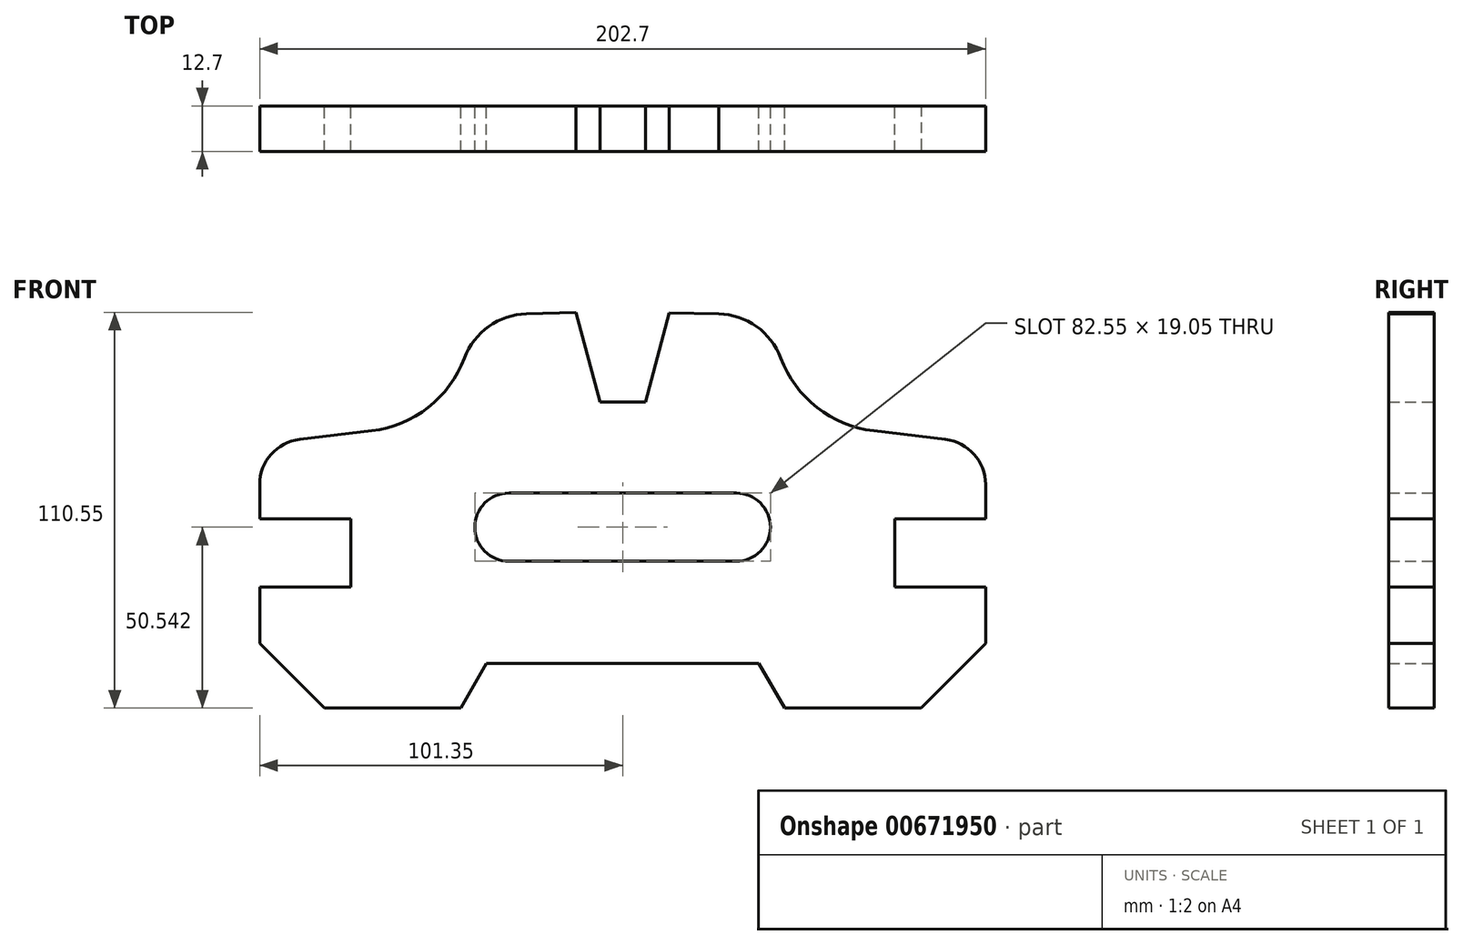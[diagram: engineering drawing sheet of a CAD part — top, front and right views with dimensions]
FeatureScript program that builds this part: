
annotation { "Feature Type Name" : "Feature", "Feature Type Description" : "" }
export const myFeature = defineFeature(function(context is Context, id is Id, definition is map)
    precondition{}
    {
        {
            var Q0;
            Q0=qCreatedBy(makeId("Front.planeOp"),FACE);
            var sketch = newSketch(context, id + "F0", { "sketchPlane" : qUnion([Q0])});
            skLineSegment(sketch, "E0", {"start": v(0, 64.43) * mm, "end": v(0, -63.1) * mm, "construction": true});
            skLineSegment(sketch, "E1", {"start": v(38.03, -38.44) * mm, "end": v(45.21, -50.88) * mm});
            skLineSegment(sketch, "E2", {"start": v(45.21, -50.88) * mm, "end": v(101.35, -50.88) * mm});
            skLineSegment(sketch, "E3", {"start": v(101.35, -50.88) * mm, "end": v(101.35, -17.1) * mm});
            skLineSegment(sketch, "E4", {"start": v(101.35, -17.1) * mm, "end": v(75.95, -17.1) * mm});
            skLineSegment(sketch, "E5", {"start": v(75.95, -17.1) * mm, "end": v(75.95, 1.95) * mm});
            skLineSegment(sketch, "E6", {"start": v(75.95, 1.95) * mm, "end": v(101.35, 1.95) * mm});
            skLineSegment(sketch, "E7", {"start": v(101.35, 1.95) * mm, "end": v(101.35, 11.6) * mm});
            skLineSegment(sketch, "E8", {"start": v(38.03, -38.44) * mm, "end": v(0, -38.44) * mm});
            skLineSegment(sketch, "E9", {"start": v(0, 9.19) * mm, "end": v(31.75, 9.19) * mm});
            skLineSegment(sketch, "E10", {"start": v(0, -9.86) * mm, "end": v(31.75, -9.86) * mm});
            skLineSegment(sketch, "E11.MirrorCS", {"start": v(-101.35, 1.95) * mm, "end": v(-101.35, 11.6) * mm});
            skLineSegment(sketch, "E12.MirrorCS", {"start": v(-75.95, 1.95) * mm, "end": v(-101.35, 1.95) * mm});
            skLineSegment(sketch, "E13.MirrorCS", {"start": v(-75.95, -17.1) * mm, "end": v(-75.95, 1.95) * mm});
            skLineSegment(sketch, "E14.MirrorCS", {"start": v(-101.35, -17.1) * mm, "end": v(-75.95, -17.1) * mm});
            skLineSegment(sketch, "E15.MirrorCS", {"start": v(-101.35, -50.88) * mm, "end": v(-101.35, -17.1) * mm});
            skLineSegment(sketch, "E16.MirrorCS", {"start": v(-45.21, -50.88) * mm, "end": v(-101.35, -50.88) * mm});
            skLineSegment(sketch, "E17.MirrorCS", {"start": v(-38.03, -38.44) * mm, "end": v(-45.21, -50.88) * mm});
            skLineSegment(sketch, "E18.MirrorCS", {"start": v(-38.03, -38.44) * mm, "end": v(0, -38.44) * mm});
            skLineSegment(sketch, "E19.MirrorCS", {"start": v(0, -9.86) * mm, "end": v(-31.75, -9.86) * mm});
            skLineSegment(sketch, "E20.MirrorCS", {"start": v(0, 9.19) * mm, "end": v(-31.75, 9.19) * mm});
            skArc(sketch, "E21", {"start": v(-31.75, 9.19) * mm, "mid": v(-41.27, -0.34) * mm, "end": v(-31.75, -9.86) * mm});
            skArc(sketch, "E22", {"start": v(31.75, -9.86) * mm, "mid": v(41.27, -0.34) * mm, "end": v(31.75, 9.19) * mm});
            skLineSegment(sketch, "E23", {"start": v(0, 34.64) * mm, "end": v(6.35, 34.64) * mm});
            skLineSegment(sketch, "E24.MirrorCS", {"start": v(0, 34.64) * mm, "end": v(-6.35, 34.64) * mm});
            skLineSegment(sketch, "E25", {"start": v(6.35, 34.64) * mm, "end": v(6.35, 73.1) * mm, "construction": true});
            skLineSegment(sketch, "E26", {"start": v(-6.35, 34.64) * mm, "end": v(-6.35, 69.53) * mm, "construction": true});
            skLineSegment(sketch, "E27", {"start": v(38.03, -38.44) * mm, "end": v(38.03, -60.96) * mm, "construction": true});
            skLineSegment(sketch, "E28.MirrorCS", {"start": v(13.01, 59.51) * mm, "end": v(6.35, 34.64) * mm});
            skLineSegment(sketch, "E29.MirrorCS", {"start": v(-13.06, 59.67) * mm, "end": v(-6.35, 34.64) * mm});
            skLineSegment(sketch, "E30", {"start": v(-26.86, 59.28) * mm, "end": v(-13.06, 59.67) * mm});
            skLineSegment(sketch, "E31", {"start": v(13.01, 59.51) * mm, "end": v(26.86, 59.28) * mm});
            skArc(sketch, "E32", {"start": v(-101.35, 11.6) * mm, "mid": v(-98.14, 20.03) * mm, "end": v(-90.15, 24.21) * mm});
            skLineSegment(sketch, "E33", {"start": v(-90.15, 24.21) * mm, "end": v(-70.1, 26.6) * mm});
            skArc(sketch, "E34", {"start": v(-70.1, 26.6) * mm, "mid": v(-54.28, 33.14) * mm, "end": v(-44.15, 46.95) * mm});
            skArc(sketch, "E35", {"start": v(-44.15, 46.95) * mm, "mid": v(-37.38, 55.75) * mm, "end": v(-26.86, 59.28) * mm});
            skArc(sketch, "E36.MirrorCS", {"start": v(101.35, 11.6) * mm, "mid": v(98.14, 20.03) * mm, "end": v(90.15, 24.21) * mm});
            skLineSegment(sketch, "E37.MirrorCS", {"start": v(90.15, 24.21) * mm, "end": v(70.1, 26.6) * mm});
            skArc(sketch, "E38.MirrorCS", {"start": v(70.1, 26.6) * mm, "mid": v(54.28, 33.14) * mm, "end": v(44.15, 46.95) * mm});
            skArc(sketch, "E39.MirrorCS", {"start": v(44.15, 46.95) * mm, "mid": v(37.38, 55.75) * mm, "end": v(26.86, 59.28) * mm});
            skSolve(sketch);
        }
        {
            var Q0;
            Q0=makeQuery(id+"F0.imprint","IMPRINT",FACE,{"disambiguationData":[TD([[makeQuery(id+"F0.imprint","IMPRINT",EDGE,{"derivedFrom":sQuery(id+"F0.wireOp",EDGE,"E1")}),1.0]])]});
            extrude(context, id + "F1", {"entities" : qUnion([Q0]), "depth" : 12.7 * mm, "offsetDistance" : 25.4 * mm});
        }
        {
            var Q0;
            Q0=makeQuery(id+"F1.opExtrude","SWEPT_EDGE",EDGE,{"disambiguationData":[OSD([sQuery(id+"F0.wireOp",EDGE,"E15.MirrorCS"),sQuery(id+"F0.wireOp",EDGE,"E16.MirrorCS")])]});
            var Q1;
            Q1=makeQuery(id+"F1.opExtrude","SWEPT_EDGE",EDGE,{"disambiguationData":[OSD([sQuery(id+"F0.wireOp",EDGE,"E2"),sQuery(id+"F0.wireOp",EDGE,"E3")])]});
            chamfer(context, id + "F2", {"entities" : qUnion([Q0, Q1]), "width" : 18.03 * mm, "tangentPropagation" : true});
        }
    });
